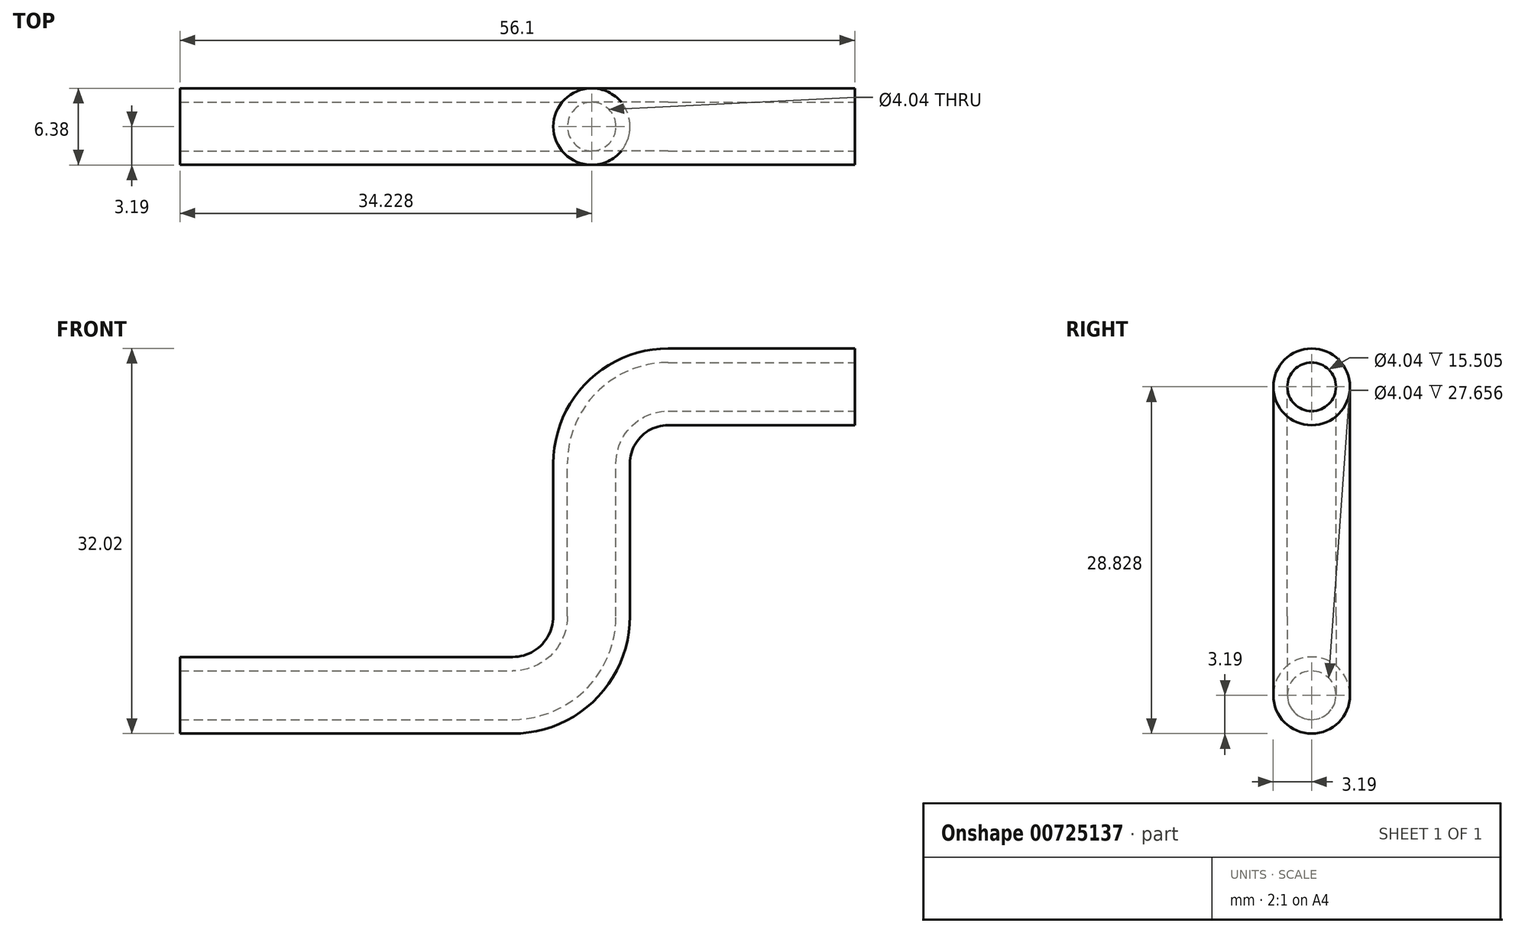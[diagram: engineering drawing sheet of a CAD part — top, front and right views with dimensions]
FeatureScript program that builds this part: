
annotation { "Feature Type Name" : "Feature", "Feature Type Description" : "" }
export const myFeature = defineFeature(function(context is Context, id is Id, definition is map)
    precondition{}
    {
        {
            var Q0;
            Q0=qCreatedBy(makeId("Right.planeOp"),FACE);
            var sketch = newSketch(context, id + "F0", { "sketchPlane" : qUnion([Q0])});
            skCircle(sketch, "E0", {"center": v(0, 0) * mm, "radius": 3.19 * mm});
            skCircle(sketch, "E1", {"center": v(0, 0) * mm, "radius": 2.02 * mm});
            skSolve(sketch);
        }
        {
            var Q0;
            Q0=qCreatedBy(makeId("Front.planeOp"),FACE);
            var sketch = newSketch(context, id + "F1", { "sketchPlane" : qUnion([Q0])});
            skLineSegment(sketch, "E2", {"start": v(0, 0) * mm, "end": v(27.66, 0) * mm});
            skArc(sketch, "E3", {"start": v(27.66, 0) * mm, "mid": v(32.3, 1.92) * mm, "end": v(34.23, 6.57) * mm});
            skPoint(sketch, "E4.orphan", {"position": v(27.66, 13.14) * mm});
            skLineSegment(sketch, "E5", {"start": v(34.23, 6.57) * mm, "end": v(34.23, 19.27) * mm});
            skArc(sketch, "E6", {"start": v(40.6, 25.64) * mm, "mid": v(36.1, 23.77) * mm, "end": v(34.23, 19.27) * mm});
            skLineSegment(sketch, "E7", {"start": v(40.6, 25.64) * mm, "end": v(56.1, 25.64) * mm});
            skPoint(sketch, "E8.orphan", {"position": v(46.96, 19.27) * mm});
            skSolve(sketch);
        }
        {
            var Q0;
            Q0=makeQuery(id+"F0.imprint","IMPRINT",FACE,{"disambiguationData":[TD([[makeQuery(id+"F0.imprint","IMPRINT",EDGE,{"derivedFrom":sQuery(id+"F0.wireOp",EDGE,"E0")}),1.0]])]});
            var Q1;
            Q1=sQuery(id+"F1.wireOp",EDGE,"E2");
            var Q2;
            Q2=sQuery(id+"F1.wireOp",EDGE,"E3");
            var Q3;
            Q3=sQuery(id+"F1.wireOp",EDGE,"E5");
            var Q4;
            Q4=sQuery(id+"F1.wireOp",EDGE,"E6");
            var Q5;
            Q5=sQuery(id+"F1.wireOp",EDGE,"E7");
            sweep(context, id + "F2", {"profiles" : qUnion([Q0]), "path" : qUnion([Q1, Q2, Q3, Q4, Q5])});
        }
    });
